# Revit family: HL_Трап для балконов и террас_HL90-3020
name_source: partatom
category: Instalační zařizovací předměty
units: mm (PartAtom-declared; Revit-internal decimal feet)

## family parameters
Bod výpočtu místnosti = Ano
Kóta kulaté spojky = Použít průměr
Nadpis OmniClass = Deck Waste Water Drains
Ořezat dutým tvarem při načtení = Ne
Sdílené = Ne
Typ dílu = Normální
Vždy vertikální = Ano
Založené na pracovní rovině = Ne
Číslo OmniClass = 23.70.50.21.24.14

## types (1)
- HL_Трап для балконов и террас_HL9030-20
    EAN = 9003076034482
    Indexovaná poznámka = HL90-3020
    Komentáře k typům = Трап для балконов и террас, с горизонтальным выпуском DN40/50, с надставным элементом 132х132/112х112 мм для вклеивания керамической плитки
    Model = HL90-3020
    Popis = Трап для балконов и террас
    Přípoj CW = Ne
    Přípoj HW = Ne
    Přípoj odpadních dílů = Ano
    Přípoj ventilace = Ne
    URL = http://www.hutterer-lechner.com
    Výchozí výška = 0 mm  [stored 0 ft]
    Výrobce = HL Hutterer & Lechner GmbH
    ВЕС = 0,76 kg
    ВЫСОТА МОНТАЖА = 89mm
    МАКСИМАЛЬНАЯ НАГРУЗКА КЛАССА = K3 -300kg
    МАТЕРИАЛ = PP
    НАСАДКА = 10 - 80 mm / 132 x 132 mm
    ПРОИЗВОДИТЕЛЬНОСТЬ = 0,56 l/s
    РАЗМЕР = DN40/50
    РЕШЁТКА = Edelstahl 112 x 112 mm

note: [stored X ft] marks values corroborated as IEEE doubles in the binary element streams (Revit-internal decimal feet)

## geometry (parser evidence)
native form markers: Blend x8, Sweep x17
no freeform markers — native parametric forms only
